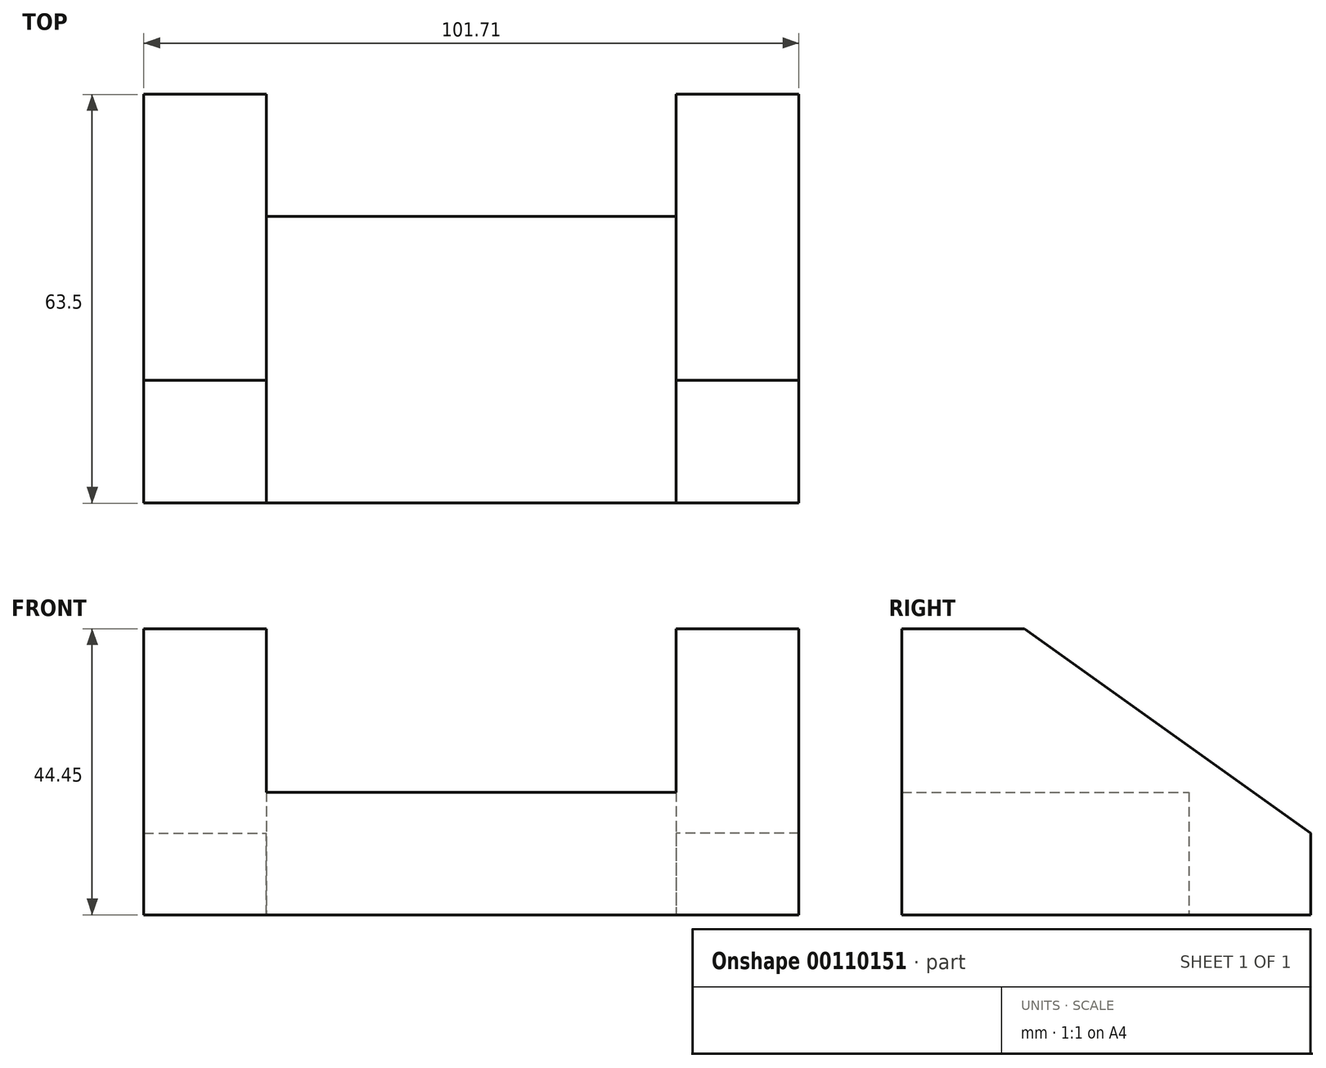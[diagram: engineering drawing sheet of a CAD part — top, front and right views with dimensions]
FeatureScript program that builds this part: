
annotation { "Feature Type Name" : "Feature", "Feature Type Description" : "" }
export const myFeature = defineFeature(function(context is Context, id is Id, definition is map)
    precondition{}
    {
        {
            var Q0;
            Q0=qCreatedBy(makeId("Top.planeOp"),FACE);
            var sketch = newSketch(context, id + "F0", { "sketchPlane" : qUnion([Q0])});
            skLineSegment(sketch, "E0", {"start": v(-53.86, 30.14) * mm, "end": v(9.75, 30.14) * mm});
            skLineSegment(sketch, "E1", {"start": v(9.75, 30.14) * mm, "end": v(9.75, -14.4) * mm});
            skLineSegment(sketch, "E2", {"start": v(9.75, -14.4) * mm, "end": v(-53.86, -14.4) * mm});
            skLineSegment(sketch, "E3", {"start": v(-53.86, -14.4) * mm, "end": v(-53.86, 30.14) * mm});
            skSolve(sketch);
        }
        {
            var Q0;
            Q0=makeQuery(id+"F0.imprint","IMPRINT",FACE,{"disambiguationData":[TD([[makeQuery(id+"F0.imprint","IMPRINT",EDGE,{"derivedFrom":sQuery(id+"F0.wireOp",EDGE,"E0")}),-1.0]])]});
            extrude(context, id + "F1", {"entities" : qUnion([Q0]), "depth" : 19.05 * mm});
        }
        {
            var Q0;
            Q0=makeQuery(id+"F1.opExtrude","SWEPT_FACE",FACE,{"disambiguationData":[OSD([sQuery(id+"F0.wireOp",EDGE,"E3")])]});
            var sketch = newSketch(context, id + "F2", { "sketchPlane" : qUnion([Q0])});
            skLineSegment(sketch, "E4", {"start": v(14.4, 0) * mm, "end": v(14.4, 44.45) * mm});
            skLineSegment(sketch, "E5", {"start": v(14.4, 0) * mm, "end": v(-49.1, 0) * mm});
            skLineSegment(sketch, "E6", {"start": v(-49.1, 0) * mm, "end": v(-49.1, 12.7) * mm});
            skLineSegment(sketch, "E7", {"start": v(14.4, 44.45) * mm, "end": v(-4.64, 44.45) * mm});
            skLineSegment(sketch, "E8", {"start": v(-4.64, 44.45) * mm, "end": v(-49.1, 12.7) * mm});
            skSolve(sketch);
        }
        {
            var Q0;
            Q0 = qSketchRegion(id + "F2", true);
            extrude(context, id + "F3", {"entities" : qUnion([Q0]), "operationType" : NewBodyOperationType.ADD, "depth" : 19.05 * mm});
        }
        {
            var Q0;
            Q0=makeQuery(id+"F1.opExtrude","SWEPT_FACE",FACE,{"disambiguationData":[OSD([sQuery(id+"F0.wireOp",EDGE,"E1")])]});
            var sketch = newSketch(context, id + "F4", { "sketchPlane" : qUnion([Q0])});
            skLineSegment(sketch, "E9", {"start": v(-14.4, 0) * mm, "end": v(-14.4, 44.45) * mm});
            skLineSegment(sketch, "E10", {"start": v(-14.4, 44.45) * mm, "end": v(4.64, 44.45) * mm});
            skLineSegment(sketch, "E11", {"start": v(4.64, 44.45) * mm, "end": v(49.1, 12.7) * mm});
            skLineSegment(sketch, "E12", {"start": v(49.1, 12.7) * mm, "end": v(49.1, 0) * mm});
            skLineSegment(sketch, "E13", {"start": v(49.1, 0) * mm, "end": v(-14.4, 0) * mm});
            skSolve(sketch);
        }
        {
            var Q0;
            {var subQ1=sQuery(id+"F4.wireOp",EDGE,"E10");Q0=makeQuery(id+"F4.imprint","IMPRINT",FACE,{"disambiguationData":[TD([[makeQuery(id+"F4.imprint","IMPRINT",EDGE,{"derivedFrom":subQ1}),-1.0]])]});}
            var Q1;
            {var subQ3=sQuery(id+"F0.wireOp",EDGE,"E1");var subQ4=makeQuery(id+"F1.opExtrude","CAP_EDGE",EDGE,{"disambiguationData":[OSD([subQ3])],"isStart":false});Q1=makeQuery(id+"F4.imprint","IMPRINT",FACE,{"disambiguationData":[TD([[makeQuery(id+"F4.imprint","IMPRINT",EDGE,{"derivedFrom":subQ4}),1.0]])]});}
            extrude(context, id + "F5", {"entities" : qUnion([Q0, Q1]), "operationType" : NewBodyOperationType.ADD, "depth" : 19.05 * mm});
        }
    });
